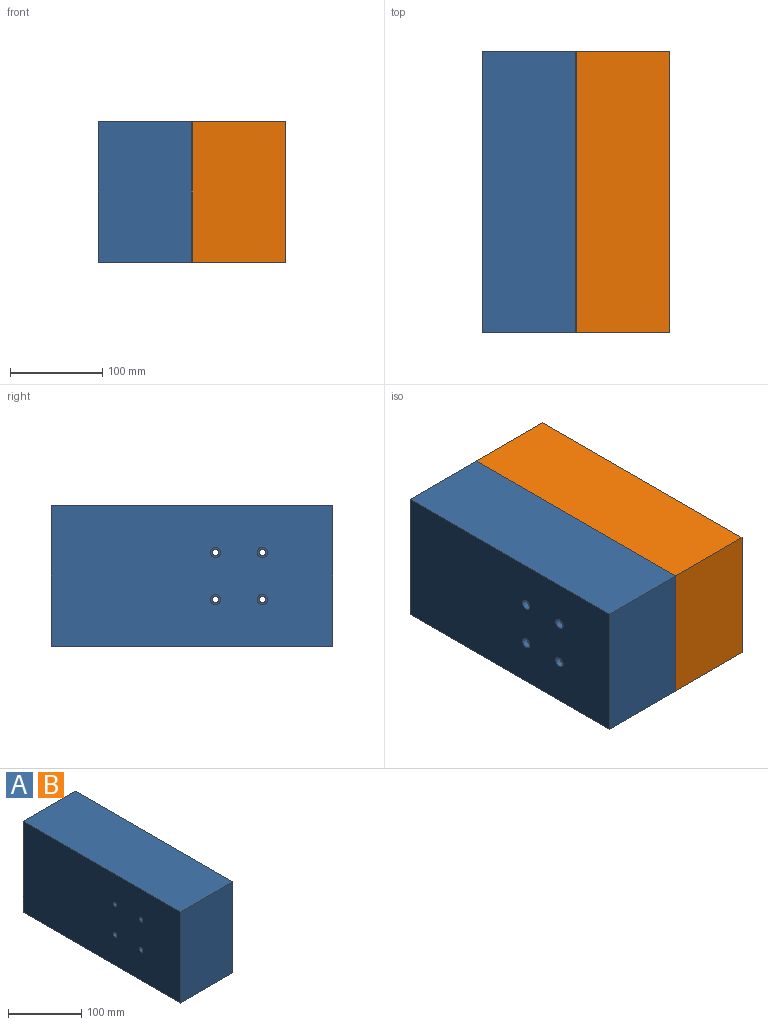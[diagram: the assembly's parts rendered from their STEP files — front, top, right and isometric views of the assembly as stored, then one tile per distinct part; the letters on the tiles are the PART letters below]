
ASSEMBLY  parts=2 mates=1
PART A: 18 faces, bbox 101.6x304.8x152.4 mm
  f0: plane 304.8x101.6mm, normal (0,0,1), area 30967.7mm2, adj f1,f3,f4,f5
  f1: plane 304.8x152.4mm, normal (-1,0,0), area 46291.5mm2, adj f0,f2,f4,f5,f6,f9,f12,f15
  f2: plane 304.8x101.6mm, normal (0,0,-1), area 30967.7mm2, adj f1,f3,f4,f5
  f3: plane 304.8x152.4mm, normal (1,0,0), area 46063.6mm2, adj f0,f2,f4,f5,f8,f11,f14,f17
  f4: plane 152.4x101.6mm, normal (0,-1,0), area 15483.8mm2, adj f0,f1,f2,f3
  f5: plane 152.4x101.6mm, normal (0,1,0), area 15483.8mm2, adj f0,f1,f2,f3
  f6: cylinder r=3.57mm len=95.25mm, axis (1,0,0), area 2135.8mm2, adj f1,f7
  f7: plane 11.11x11.11mm, normal (1,0,0), area 57mm2, adj f6,f8
  f8: cylinder r=5.56mm len=11.11mm, axis (1,0,0), area 221.7mm2, adj f3,f7
  f9: cylinder r=3.57mm len=95.25mm, axis (1,0,0), area 2135.8mm2, adj f1,f10
  f10: plane 11.11x11.11mm, normal (1,0,0), area 57mm2, adj f9,f11
  f11: cylinder r=5.56mm len=11.11mm, axis (1,0,0), area 221.7mm2, adj f3,f10
  f12: cylinder r=3.57mm len=95.25mm, axis (1,0,0), area 2135.8mm2, adj f1,f13
  f13: plane 11.11x11.11mm, normal (1,0,0), area 57mm2, adj f12,f14
  f14: cylinder r=5.56mm len=11.11mm, axis (1,0,0), area 221.7mm2, adj f3,f13
  f15: cylinder r=3.57mm len=95.25mm, axis (1,0,0), area 2135.8mm2, adj f1,f16
  f16: plane 11.11x11.11mm, normal (1,0,0), area 57mm2, adj f15,f17
  f17: cylinder r=5.56mm len=11.11mm, axis (1,0,0), area 221.7mm2, adj f3,f16
PART B: same geometry as A
PLACE A rot(axis=(0,1,0),180deg) t=(-236.65,-16.62,92.02)mm
PLACE B t=(-135.05,-16.62,92.02)mm
MATE fastened A.f1 <-> B.f1  axis (1,0,0) through (-185.85,-16.44,92.02)mm
